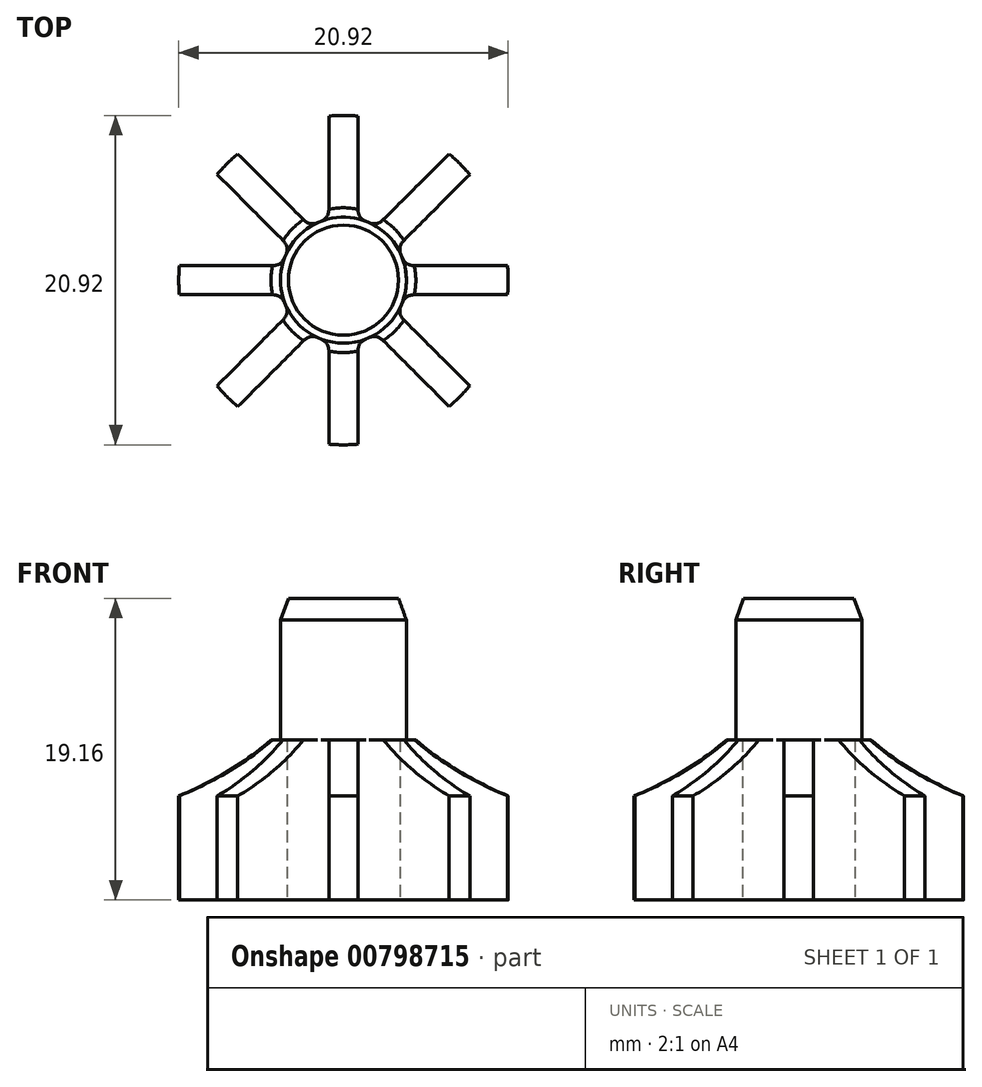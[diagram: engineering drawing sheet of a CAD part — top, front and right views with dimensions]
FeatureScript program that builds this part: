
annotation { "Feature Type Name" : "Feature", "Feature Type Description" : "" }
export const myFeature = defineFeature(function(context is Context, id is Id, definition is map)
    precondition{}
    {
        {
            var Q0;
            Q0=qCreatedBy(makeId("Top.planeOp"),FACE);
            var sketch = newSketch(context, id + "F0", { "sketchPlane" : qUnion([Q0])});
            skCircle(sketch, "E0", {"center": v(0, 0) * mm, "radius": 58.42 * mm});
            skArc(sketch, "E1", {"start": v(-57.14, -0.93) * mm, "mid": v(-52.8, -21.87) * mm, "end": v(-41.06, -39.75) * mm});
            skArc(sketch, "E2", {"start": v(-3.65, 1.64) * mm, "mid": v(-3.7, 1.53) * mm, "end": v(-3.74, 1.42) * mm});
            skLineSegment(sketch, "E3.left", {"start": v(0, 4) * mm, "end": v(0, 3.11) * mm});
            skLineSegment(sketch, "E3.right", {"start": v(0.93, 57.92) * mm, "end": v(0.93, 38.09) * mm});
            skLineSegment(sketch, "E4.MirrorCS", {"start": v(-0.93, 57.92) * mm, "end": v(-0.93, 39.36) * mm});
            skLineSegment(sketch, "E5.1.0", {"start": v(-40.3, 41.61) * mm, "end": v(-26.28, 27.59) * mm});
            skLineSegment(sketch, "E5.1.1", {"start": v(-41.61, 40.3) * mm, "end": v(-27.59, 26.28) * mm});
            skLineSegment(sketch, "E5.2.0", {"start": v(-57.92, 0.93) * mm, "end": v(-38.09, 0.93) * mm});
            skLineSegment(sketch, "E5.2.1", {"start": v(-57.92, -0.93) * mm, "end": v(-39.36, -0.93) * mm});
            skLineSegment(sketch, "E5.3.0", {"start": v(-41.61, -40.3) * mm, "end": v(-27.59, -26.28) * mm});
            skLineSegment(sketch, "E5.3.1", {"start": v(-40.3, -41.61) * mm, "end": v(-27.17, -28.49) * mm});
            skLineSegment(sketch, "E5.4.0", {"start": v(-0.93, -57.92) * mm, "end": v(-0.93, -38.09) * mm});
            skLineSegment(sketch, "E5.4.1", {"start": v(0.93, -57.92) * mm, "end": v(0.93, -39.36) * mm});
            skLineSegment(sketch, "E5.5.0", {"start": v(40.3, -41.61) * mm, "end": v(27.17, -28.49) * mm});
            skLineSegment(sketch, "E5.5.1", {"start": v(41.61, -40.3) * mm, "end": v(27.59, -26.28) * mm});
            skLineSegment(sketch, "E5.6.0", {"start": v(57.92, -0.93) * mm, "end": v(38.09, -0.93) * mm});
            skLineSegment(sketch, "E5.6.1", {"start": v(57.92, 0.93) * mm, "end": v(39.36, 0.93) * mm});
            skLineSegment(sketch, "E5.7.0", {"start": v(41.61, 40.3) * mm, "end": v(28.49, 27.17) * mm});
            skLineSegment(sketch, "E5.7.1", {"start": v(40.3, 41.61) * mm, "end": v(26.28, 27.59) * mm});
            skArc(sketch, "E6.trimOffspring", {"start": v(-39.75, -41.06) * mm, "mid": v(-21.87, -52.8) * mm, "end": v(-0.93, -57.14) * mm});
            skArc(sketch, "E7.trimOffspring", {"start": v(0.93, -57.14) * mm, "mid": v(21.87, -52.8) * mm, "end": v(39.75, -41.06) * mm});
            skArc(sketch, "E8.trimOffspring", {"start": v(41.06, -39.75) * mm, "mid": v(52.8, -21.87) * mm, "end": v(57.14, -0.93) * mm});
            skArc(sketch, "E9.trimOffspring", {"start": v(57.14, 0.93) * mm, "mid": v(52.8, 21.87) * mm, "end": v(41.06, 39.75) * mm});
            skArc(sketch, "E10.trimOffspring", {"start": v(39.75, 41.06) * mm, "mid": v(21.87, 52.8) * mm, "end": v(0.93, 57.14) * mm});
            skArc(sketch, "E11.trimOffspring", {"start": v(-0.93, 57.14) * mm, "mid": v(-21.87, 52.8) * mm, "end": v(-39.75, 41.06) * mm});
            skPoint(sketch, "E12.orphan", {"position": v(0, 57.15) * mm});
            skArc(sketch, "E13.trimOffspring", {"start": v(-41.06, 39.75) * mm, "mid": v(-52.8, 21.87) * mm, "end": v(-57.14, 0.93) * mm});
            skArc(sketch, "E14.trimOffspring", {"start": v(-3.74, -1.42) * mm, "mid": v(-3.7, -1.53) * mm, "end": v(-3.65, -1.64) * mm});
            skArc(sketch, "E15.trimOffspring", {"start": v(-1.64, -3.65) * mm, "mid": v(-1.53, -3.7) * mm, "end": v(-1.42, -3.74) * mm});
            skArc(sketch, "E16.trimOffspring", {"start": v(1.42, -3.74) * mm, "mid": v(1.53, -3.7) * mm, "end": v(1.64, -3.65) * mm});
            skArc(sketch, "E17.trimOffspring", {"start": v(3.65, -1.64) * mm, "mid": v(3.7, -1.53) * mm, "end": v(3.74, -1.42) * mm});
            skArc(sketch, "E18.trimOffspring", {"start": v(3.74, 1.42) * mm, "mid": v(3.7, 1.53) * mm, "end": v(3.65, 1.64) * mm});
            skArc(sketch, "E19.trimOffspring", {"start": v(1.64, 3.65) * mm, "mid": v(1.53, 3.7) * mm, "end": v(1.42, 3.74) * mm});
            skArc(sketch, "E20.trimOffspring", {"start": v(-1.42, 3.74) * mm, "mid": v(-1.53, 3.7) * mm, "end": v(-1.64, 3.65) * mm});
            skPoint(sketch, "E21.visualSharp", {"position": v(-3.4, 2.1) * mm});
            skArc(sketch, "E21.filletArc", {"start": v(-3.65, 1.64) * mm, "mid": v(-3.6, 2.1) * mm, "end": v(-3.8, 2.5) * mm});
            skPoint(sketch, "E22.visualSharp", {"position": v(-3.9, 0.93) * mm});
            skArc(sketch, "E22.filletArc", {"start": v(-4.45, 0.93) * mm, "mid": v(-4.02, 1.06) * mm, "end": v(-3.74, 1.42) * mm});
            skPoint(sketch, "E23.visualSharp", {"position": v(-3.9, -0.93) * mm});
            skArc(sketch, "E23.filletArc", {"start": v(-3.74, -1.42) * mm, "mid": v(-4.02, -1.06) * mm, "end": v(-4.45, -0.93) * mm});
            skPoint(sketch, "E24.visualSharp", {"position": v(-3.4, -2.1) * mm});
            skArc(sketch, "E24.filletArc", {"start": v(-3.8, -2.5) * mm, "mid": v(-3.6, -2.1) * mm, "end": v(-3.65, -1.64) * mm});
            skPoint(sketch, "E25.visualSharp", {"position": v(-2.1, -3.4) * mm});
            skArc(sketch, "E25.filletArc", {"start": v(-1.64, -3.65) * mm, "mid": v(-2.1, -3.6) * mm, "end": v(-2.5, -3.8) * mm});
            skPoint(sketch, "E26.visualSharp", {"position": v(-0.93, -3.9) * mm});
            skArc(sketch, "E26.filletArc", {"start": v(-0.93, -4.45) * mm, "mid": v(-1.06, -4.02) * mm, "end": v(-1.42, -3.74) * mm});
            skPoint(sketch, "E27.visualSharp", {"position": v(0.93, -3.9) * mm});
            skArc(sketch, "E27.filletArc", {"start": v(1.42, -3.74) * mm, "mid": v(1.06, -4.02) * mm, "end": v(0.93, -4.45) * mm});
            skPoint(sketch, "E28.visualSharp", {"position": v(2.1, -3.4) * mm});
            skArc(sketch, "E28.filletArc", {"start": v(2.5, -3.8) * mm, "mid": v(2.1, -3.6) * mm, "end": v(1.64, -3.65) * mm});
            skPoint(sketch, "E29.visualSharp", {"position": v(3.4, -2.1) * mm});
            skArc(sketch, "E29.filletArc", {"start": v(3.65, -1.64) * mm, "mid": v(3.6, -2.1) * mm, "end": v(3.8, -2.5) * mm});
            skPoint(sketch, "E30.visualSharp", {"position": v(3.9, -0.93) * mm});
            skArc(sketch, "E30.filletArc", {"start": v(4.45, -0.93) * mm, "mid": v(4.02, -1.06) * mm, "end": v(3.74, -1.42) * mm});
            skPoint(sketch, "E31.visualSharp", {"position": v(3.9, 0.93) * mm});
            skArc(sketch, "E31.filletArc", {"start": v(3.74, 1.42) * mm, "mid": v(4.02, 1.06) * mm, "end": v(4.45, 0.93) * mm});
            skPoint(sketch, "E32.visualSharp", {"position": v(3.4, 2.1) * mm});
            skArc(sketch, "E32.filletArc", {"start": v(3.8, 2.5) * mm, "mid": v(3.6, 2.1) * mm, "end": v(3.65, 1.64) * mm});
            skPoint(sketch, "E33.visualSharp", {"position": v(2.1, 3.4) * mm});
            skArc(sketch, "E33.filletArc", {"start": v(1.64, 3.65) * mm, "mid": v(2.1, 3.6) * mm, "end": v(2.5, 3.8) * mm});
            skPoint(sketch, "E34.visualSharp", {"position": v(0.93, 3.9) * mm});
            skArc(sketch, "E34.filletArc", {"start": v(0.93, 4.45) * mm, "mid": v(1.06, 4.02) * mm, "end": v(1.42, 3.74) * mm});
            skPoint(sketch, "E35.visualSharp", {"position": v(-0.93, 3.9) * mm});
            skArc(sketch, "E35.filletArc", {"start": v(-1.42, 3.74) * mm, "mid": v(-1.06, 4.02) * mm, "end": v(-0.93, 4.45) * mm});
            skPoint(sketch, "E36.visualSharp", {"position": v(-2.1, 3.4) * mm});
            skArc(sketch, "E36.filletArc", {"start": v(-2.5, 3.8) * mm, "mid": v(-2.1, 3.6) * mm, "end": v(-1.64, 3.65) * mm});
            skLineSegment(sketch, "E37.trimOffspring", {"start": v(26.28, 27.59) * mm, "end": v(2.5, 3.8) * mm});
            skLineSegment(sketch, "E38.trimOffspring", {"start": v(28.49, 27.17) * mm, "end": v(3.8, 2.5) * mm});
            skLineSegment(sketch, "E39.trimOffspring", {"start": v(39.36, 0.93) * mm, "end": v(4.45, 0.93) * mm});
            skLineSegment(sketch, "E40.trimOffspring", {"start": v(38.09, -0.93) * mm, "end": v(4.45, -0.93) * mm});
            skLineSegment(sketch, "E41.trimOffspring", {"start": v(-26.28, 27.59) * mm, "end": v(-2.5, 3.8) * mm});
            skLineSegment(sketch, "E42.trimOffspring", {"start": v(-27.59, 26.28) * mm, "end": v(-3.8, 2.5) * mm});
            skLineSegment(sketch, "E43.trimOffspring", {"start": v(-0.93, 39.36) * mm, "end": v(-0.93, 4.45) * mm});
            skLineSegment(sketch, "E44.trimOffspring", {"start": v(0.93, 38.09) * mm, "end": v(0.93, 4.45) * mm});
            skLineSegment(sketch, "E45.trimOffspring", {"start": v(-39.36, -0.93) * mm, "end": v(-4.45, -0.93) * mm});
            skLineSegment(sketch, "E46.trimOffspring", {"start": v(-38.09, 0.93) * mm, "end": v(-4.45, 0.93) * mm});
            skLineSegment(sketch, "E47.trimOffspring", {"start": v(-27.59, -26.28) * mm, "end": v(-3.8, -2.5) * mm});
            skLineSegment(sketch, "E48.trimOffspring", {"start": v(-27.17, -28.49) * mm, "end": v(-2.5, -3.8) * mm});
            skLineSegment(sketch, "E49.trimOffspring", {"start": v(-0.93, -38.09) * mm, "end": v(-0.93, -4.45) * mm});
            skLineSegment(sketch, "E50.trimOffspring", {"start": v(0.93, -39.36) * mm, "end": v(0.93, -4.45) * mm});
            skLineSegment(sketch, "E51.trimOffspring", {"start": v(27.59, -26.28) * mm, "end": v(3.8, -2.5) * mm});
            skLineSegment(sketch, "E52.trimOffspring", {"start": v(27.17, -28.49) * mm, "end": v(2.5, -3.8) * mm});
            skSolve(sketch);
        }
        {
            var Q0;
            Q0=makeQuery(id+"F0.imprint","IMPRINT",FACE,{"disambiguationData":[TD([[makeQuery(id+"F0.imprint","IMPRINT",EDGE,{"derivedFrom":sQuery(id+"F0.wireOp",EDGE,"E0")}),1.0]])]});
            extrude(context, id + "F1", {"entities" : qUnion([Q0]), "depth" : 10.16 * mm, "offsetDistance" : 25.4 * mm});
        }
        {
            var Q0;
            Q0=qCreatedBy(makeId("Top.planeOp"),FACE);
            var sketch = newSketch(context, id + "F2", { "sketchPlane" : qUnion([Q0])});
            skCircle(sketch, "E53", {"center": v(0, 0) * mm, "radius": 58.42 * mm});
            skCircle(sketch, "E54", {"center": v(0, 0) * mm, "radius": 36.83 * mm});
            skSolve(sketch);
        }
        {
            var Q0;
            Q0=qSketchRegion(id+"F2",true);
            extrude(context, id + "F3", {"entities" : qUnion([Q0]), "operationType" : NewBodyOperationType.ADD, "depth" : .4 * mm, "offsetDistance" : 25.4 * mm});
        }
        {
            var Q0;
            Q0=qCreatedBy(makeId("Right.planeOp"),FACE);
            var sketch = newSketch(context, id + "F4", { "sketchPlane" : qUnion([Q0])});
            skLineSegment(sketch, "E55.bottom", {"start": v(0, 24.07) * mm, "end": v(59.85, 24.07) * mm});
            skLineSegment(sketch, "E55.left", {"start": v(0, 24.07) * mm, "end": v(0, 16.63) * mm});
            skLineSegment(sketch, "E55.right", {"start": v(59.85, 24.07) * mm, "end": v(59.85, 0) * mm});
            skPoint(sketch, "E55.top.start.orphan", {"position": v(0, 9.19) * mm});
            skFitSpline(sketch, "E56", {"points": [v(0, 16.63) * mm, v(12.4, 5.88) * mm, v(52.4, 2.04) * mm, v(59.85, 0) * mm], "startDerivative": vector(15.3, -40.46) * mm, "endDerivative": vector(19.52, -15.16) * mm});
            skLineSegment(sketch, "E57.top", {"start": v(36.88, 0) * mm, "end": v(38.1, 0) * mm});
            skLineSegment(sketch, "E58", {"start": v(0, 0) * mm, "end": v(38.1, 0) * mm});
            skSolve(sketch);
        }
        {
            var Q0;
            Q0=makeQuery(id+"F4.imprint","IMPRINT",FACE,{"disambiguationData":[TD([[makeQuery(id+"F4.imprint","IMPRINT",EDGE,{"derivedFrom":sQuery(id+"F4.wireOp",EDGE,"E57.bottom")}),-1.0]])]});
            var Q1;
            Q1=makeQuery(id+"F4.imprint","IMPRINT",FACE,{"disambiguationData":[TD([[makeQuery(id+"F4.imprint","IMPRINT",EDGE,{"derivedFrom":sQuery(id+"F4.wireOp",EDGE,"E55.bottom")}),-1.0]])]});
            var Q2;
            Q2=makeQuery(id+"F1.opExtrude","SWEPT_FACE",FACE,{"disambiguationData":[OSD([sQuery(id+"F0.wireOp",EDGE,"E0")])]});
            revolve(context, id + "F5", {"operationType" : NewBodyOperationType.REMOVE, "surfaceOperationType" : NewSurfaceOperationType.NEW, "entities" : qUnion([Q0, Q1]), "axis" : qUnion([Q2]), "revolveType" : RevolveType.FULL, "oppositeDirection" : true});
        }
        {
            var Q0;
            Q0=makeQuery(id+"F1.opExtrude","CAP_FACE",FACE,{"disambiguationData":[OSD([sQuery(id+"F0.wireOp",EDGE,"E0"),sQuery(id+"F0.wireOp",EDGE,"E1"),sQuery(id+"F0.wireOp",EDGE,"E2"),sQuery(id+"F0.wireOp",EDGE,"E3.right"),sQuery(id+"F0.wireOp",EDGE,"E4.MirrorCS"),sQuery(id+"F0.wireOp",EDGE,"E5.1.0"),sQuery(id+"F0.wireOp",EDGE,"E5.1.1"),sQuery(id+"F0.wireOp",EDGE,"E5.2.0"),sQuery(id+"F0.wireOp",EDGE,"E5.2.1"),sQuery(id+"F0.wireOp",EDGE,"E5.3.0"),sQuery(id+"F0.wireOp",EDGE,"E5.3.1"),sQuery(id+"F0.wireOp",EDGE,"E5.4.0"),sQuery(id+"F0.wireOp",EDGE,"E5.4.1"),sQuery(id+"F0.wireOp",EDGE,"E5.5.0"),sQuery(id+"F0.wireOp",EDGE,"E5.5.1"),sQuery(id+"F0.wireOp",EDGE,"E5.6.0"),sQuery(id+"F0.wireOp",EDGE,"E5.6.1"),sQuery(id+"F0.wireOp",EDGE,"E5.7.0"),sQuery(id+"F0.wireOp",EDGE,"E5.7.1"),sQuery(id+"F0.wireOp",EDGE,"E6.trimOffspring"),sQuery(id+"F0.wireOp",EDGE,"E7.trimOffspring"),sQuery(id+"F0.wireOp",EDGE,"E8.trimOffspring"),sQuery(id+"F0.wireOp",EDGE,"E9.trimOffspring"),sQuery(id+"F0.wireOp",EDGE,"E10.trimOffspring"),sQuery(id+"F0.wireOp",EDGE,"E11.trimOffspring"),sQuery(id+"F0.wireOp",EDGE,"E13.trimOffspring"),sQuery(id+"F0.wireOp",EDGE,"E14.trimOffspring"),sQuery(id+"F0.wireOp",EDGE,"E15.trimOffspring"),sQuery(id+"F0.wireOp",EDGE,"E16.trimOffspring"),sQuery(id+"F0.wireOp",EDGE,"E17.trimOffspring"),sQuery(id+"F0.wireOp",EDGE,"E18.trimOffspring"),sQuery(id+"F0.wireOp",EDGE,"E19.trimOffspring"),sQuery(id+"F0.wireOp",EDGE,"E20.trimOffspring"),sQuery(id+"F0.wireOp",EDGE,"E21.filletArc"),sQuery(id+"F0.wireOp",EDGE,"E22.filletArc"),sQuery(id+"F0.wireOp",EDGE,"E23.filletArc"),sQuery(id+"F0.wireOp",EDGE,"E24.filletArc"),sQuery(id+"F0.wireOp",EDGE,"E25.filletArc"),sQuery(id+"F0.wireOp",EDGE,"E26.filletArc"),sQuery(id+"F0.wireOp",EDGE,"E27.filletArc"),sQuery(id+"F0.wireOp",EDGE,"E28.filletArc"),sQuery(id+"F0.wireOp",EDGE,"E29.filletArc"),sQuery(id+"F0.wireOp",EDGE,"E30.filletArc"),sQuery(id+"F0.wireOp",EDGE,"E31.filletArc"),sQuery(id+"F0.wireOp",EDGE,"E32.filletArc"),sQuery(id+"F0.wireOp",EDGE,"E33.filletArc"),sQuery(id+"F0.wireOp",EDGE,"E34.filletArc"),sQuery(id+"F0.wireOp",EDGE,"E35.filletArc"),sQuery(id+"F0.wireOp",EDGE,"E36.filletArc"),sQuery(id+"F0.wireOp",EDGE,"E37.trimOffspring"),sQuery(id+"F0.wireOp",EDGE,"E38.trimOffspring"),sQuery(id+"F0.wireOp",EDGE,"E39.trimOffspring"),sQuery(id+"F0.wireOp",EDGE,"E40.trimOffspring"),sQuery(id+"F0.wireOp",EDGE,"E41.trimOffspring"),sQuery(id+"F0.wireOp",EDGE,"E42.trimOffspring"),sQuery(id+"F0.wireOp",EDGE,"E43.trimOffspring"),sQuery(id+"F0.wireOp",EDGE,"E44.trimOffspring"),sQuery(id+"F0.wireOp",EDGE,"E45.trimOffspring"),sQuery(id+"F0.wireOp",EDGE,"E46.trimOffspring"),sQuery(id+"F0.wireOp",EDGE,"E47.trimOffspring"),sQuery(id+"F0.wireOp",EDGE,"E48.trimOffspring"),sQuery(id+"F0.wireOp",EDGE,"E49.trimOffspring"),sQuery(id+"F0.wireOp",EDGE,"E50.trimOffspring"),sQuery(id+"F0.wireOp",EDGE,"E51.trimOffspring"),sQuery(id+"F0.wireOp",EDGE,"E52.trimOffspring")])],"isStart":false});
            var sketch = newSketch(context, id + "F6", { "sketchPlane" : qUnion([Q0])});
            skCircle(sketch, "E59", {"center": v(0, 0) * mm, "radius": 4 * mm});
            skSolve(sketch);
        }
        {
            var Q0;
            {var subQ0=sQuery(id+"F6.wireOp",EDGE,"E59");var subQ4=makeQuery(id+"F6.imprint","INTERSECT",VERTEX,{"derivedFrom":[makeQuery(id+"F1.opExtrude","CAP_EDGE",EDGE,{"disambiguationData":[OSD([sQuery(id+"F0.wireOp",EDGE,"E33.filletArc")])],"isStart":false}),subQ0]});Q0=makeQuery(id+"F6.imprint","IMPRINT",FACE,{"disambiguationData":[TD([[makeQuery(id+"F6.imprint","IMPRINT",EDGE,{"disambiguationData":[TD([[subQ4,-1.0]])],"derivedFrom":subQ0}),1.0]])]});}
            extrude(context, id + "F7", {"entities" : qUnion([Q0]), "operationType" : NewBodyOperationType.ADD, "depth" : 9 * mm, "offsetDistance" : 25.4 * mm});
        }
        {
            var Q0;
            Q0=qCreatedBy(makeId("Top.planeOp"),FACE);
            var sketch = newSketch(context, id + "F8", { "sketchPlane" : qUnion([Q0])});
            skCircle(sketch, "E60", {"center": v(0, 0) * mm, "radius": 10.46 * mm});
            skCircle(sketch, "E61", {"center": v(0, 0) * mm, "radius": 74.97 * mm});
            skSolve(sketch);
        }
        {
            var Q0;
            Q0 = qSketchRegion(id + "F8", true);
            extrude(context, id + "F9", {"entities" : qUnion([Q0]), "operationType" : NewBodyOperationType.REMOVE, "endBound" : BoundingType.THROUGH_ALL, "depth" : 25.4 * mm, "offsetDistance" : 25.4 * mm});
        }
        {
            var Q0;
            Q0=makeQuery(id+"F7.opExtrude","CAP_EDGE",EDGE,{"disambiguationData":[OSD([sQuery(id+"F6.wireOp",EDGE,"E59")])],"isStart":false});
            chamfer(context, id + "F10", {"entities" : qUnion([Q0]), "chamferType" : ChamferType.OFFSET_ANGLE, "width" : .5 * mm, "oppositeDirection" : false, "angle" : 70 * degree, "tangentPropagation" : true});
        }
    });
